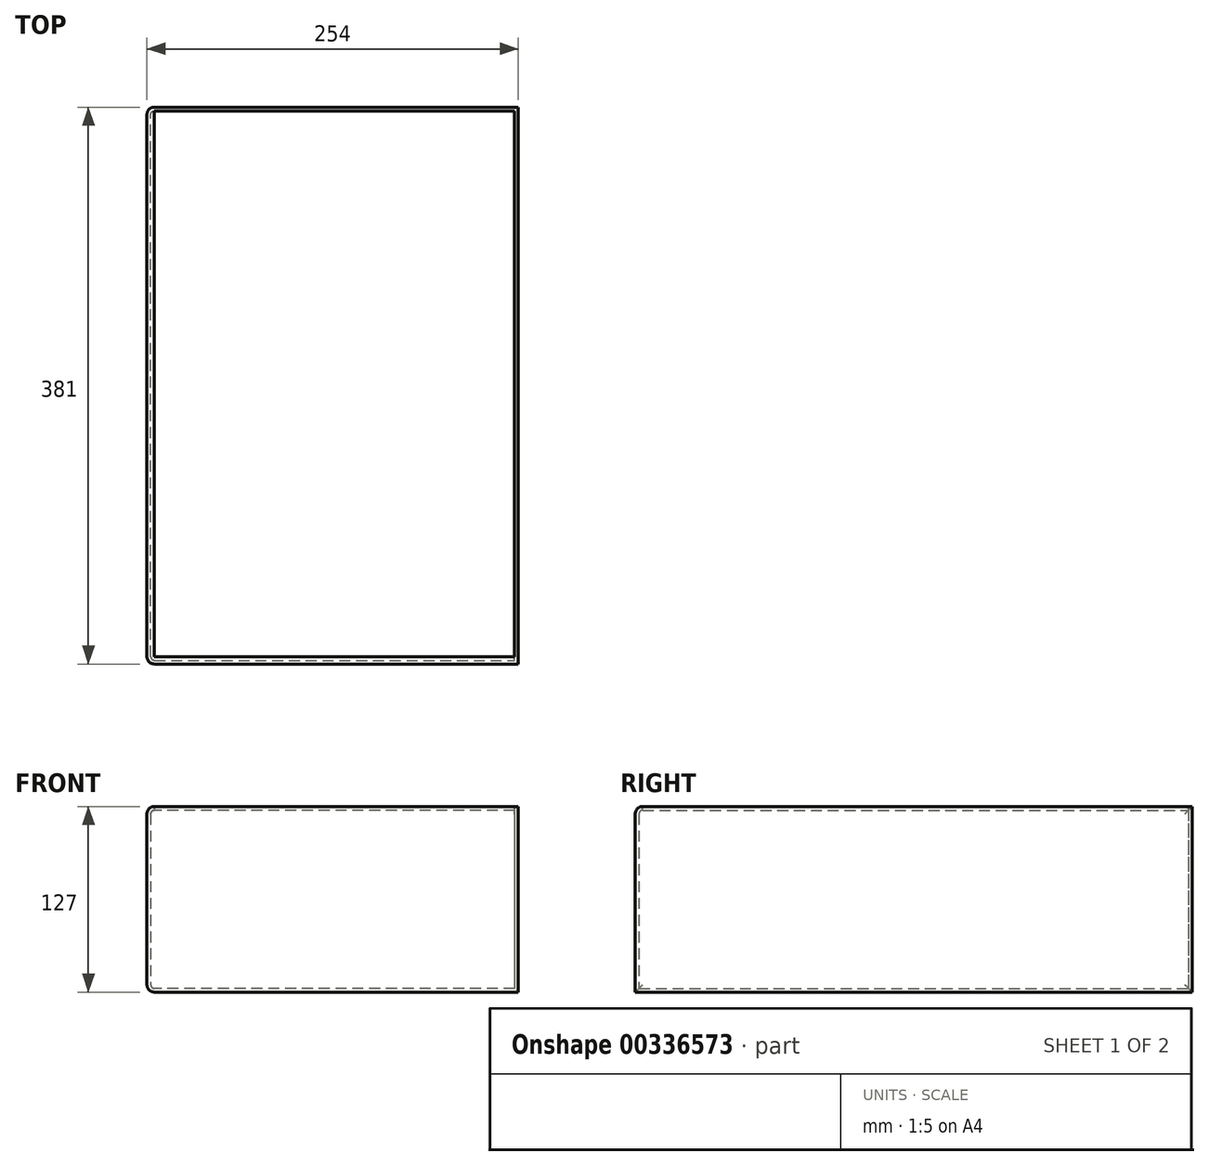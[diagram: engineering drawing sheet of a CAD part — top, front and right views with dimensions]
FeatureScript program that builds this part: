
annotation { "Feature Type Name" : "Feature", "Feature Type Description" : "" }
export const myFeature = defineFeature(function(context is Context, id is Id, definition is map)
    precondition{}
    {
        {
            var Q0;
            Q0=qCreatedBy(makeId("Top.planeOp"),FACE);
            var sketch = newSketch(context, id + "F0", { "sketchPlane" : qUnion([Q0])});
            skLineSegment(sketch, "E0", {"start": v(0, 0) * mm, "end": v(-254, 0) * mm});
            skLineSegment(sketch, "E1", {"start": v(-254, 0) * mm, "end": v(-254, -381) * mm});
            skLineSegment(sketch, "E2", {"start": v(-254, -381) * mm, "end": v(0, -381) * mm});
            skLineSegment(sketch, "E3", {"start": v(0, -381) * mm, "end": v(0, 0) * mm});
            skSolve(sketch);
        }
        {
            var Q0;
            Q0 = qSketchRegion(id + "F0", true);
            extrude(context, id + "F1", {"entities" : qUnion([Q0]), "depth" : 127 * mm});
        }
        {
            var Q0;
            Q0=makeQuery(id+"F1.opExtrude","CAP_EDGE",EDGE,{"disambiguationData":[OSD([sQuery(id+"F0.wireOp",EDGE,"E1")])],"isStart":false});
            var Q1;
            Q1=makeQuery(id+"F1.opExtrude","CAP_EDGE",EDGE,{"disambiguationData":[OSD([sQuery(id+"F0.wireOp",EDGE,"E2")])],"isStart":false});
            var Q2;
            Q2=makeQuery(id+"F1.opExtrude","SWEPT_FACE",FACE,{"disambiguationData":[OSD([sQuery(id+"F0.wireOp",EDGE,"E1")])]});
            fillet(context, id + "F2", {"entities" : qUnion([Q0, Q1, Q2]), "radius" : 5.08 * mm, "tangentPropagation" : true, "allowEdgeOverflow" : false});
        }
        {
            var Q0;
            Q0=makeQuery(id+"F1.opExtrude","CAP_FACE",FACE,{"disambiguationData":[OSD([sQuery(id+"F0.wireOp",EDGE,"E0"),sQuery(id+"F0.wireOp",EDGE,"E1"),sQuery(id+"F0.wireOp",EDGE,"E2"),sQuery(id+"F0.wireOp",EDGE,"E3")])],"isStart":false});
            shell(context, id + "F3", {"entities" : qUnion([Q0]), "thickness" : 2.54 * mm});
        }
    });
